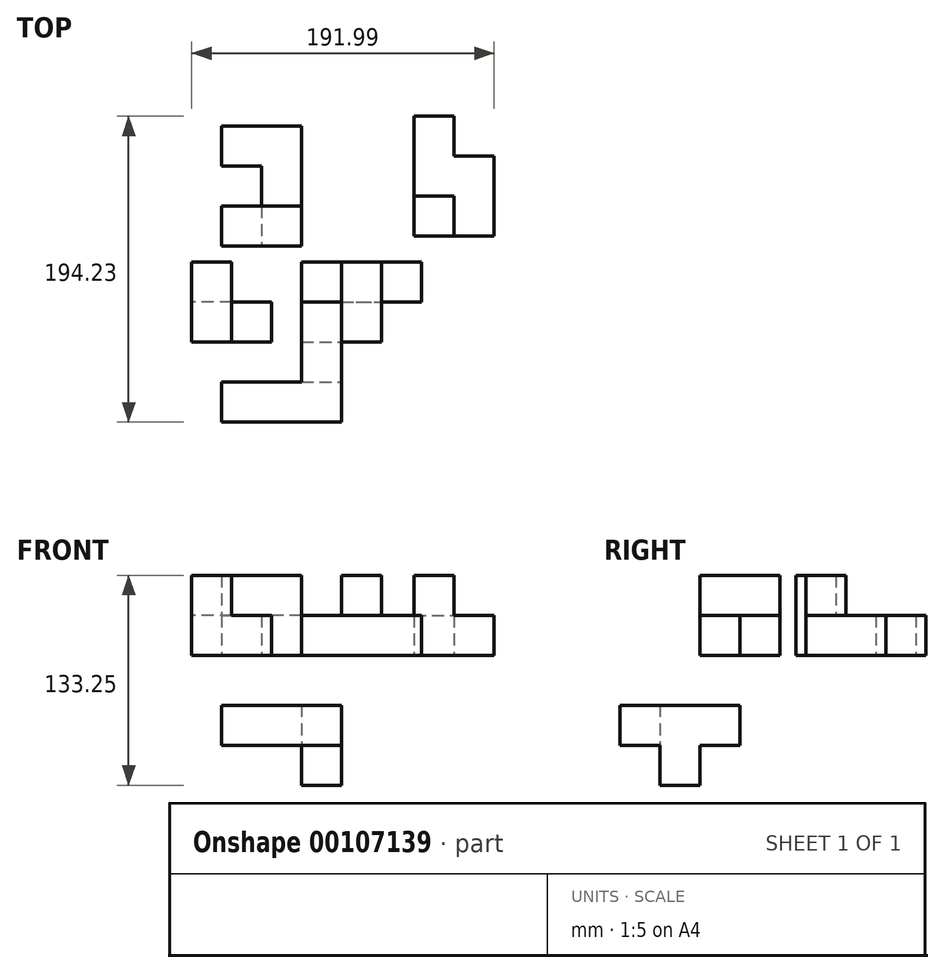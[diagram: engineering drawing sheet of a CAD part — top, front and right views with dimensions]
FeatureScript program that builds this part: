
annotation { "Feature Type Name" : "Feature", "Feature Type Description" : "" }
export const myFeature = defineFeature(function(context is Context, id is Id, definition is map)
    precondition{}
    {
        {
            var Q0;
            Q0=qCreatedBy(makeId("Front.planeOp"),FACE);
            var sketch = newSketch(context, id + "F0", { "sketchPlane" : qUnion([Q0])});
            skLineSegment(sketch, "E0.bottom", {"start": v(-69.75, 25.4) * mm, "end": v(-18.95, 25.4) * mm});
            skLineSegment(sketch, "E0.top", {"start": v(-69.75, 0) * mm, "end": v(-18.95, 0) * mm});
            skLineSegment(sketch, "E0.left", {"start": v(-69.75, 25.4) * mm, "end": v(-69.75, 0) * mm});
            skLineSegment(sketch, "E0.right", {"start": v(-18.95, 25.4) * mm, "end": v(-18.95, 0) * mm});
            skSolve(sketch);
        }
        {
            var Q0;
            Q0=makeQuery(id+"F0.imprint","IMPRINT",FACE,{"disambiguationData":[TD([[makeQuery(id+"F0.imprint","IMPRINT",EDGE,{"derivedFrom":sQuery(id+"F0.wireOp",EDGE,"E0.bottom")}),-1.0]])]});
            extrude(context, id + "F1", {"entities" : qUnion([Q0]), "depth" : 25.4 * mm});
        }
        {
            var Q0;
            Q0=makeQuery(id+"F1.opExtrude","SWEPT_FACE",FACE,{"disambiguationData":[OSD([sQuery(id+"F0.wireOp",EDGE,"E0.bottom")])]});
            var sketch = newSketch(context, id + "F2", { "sketchPlane" : qUnion([Q0])});
            skLineSegment(sketch, "E1.bottom", {"start": v(-69.75, -25.4) * mm, "end": v(-44.35, -25.4) * mm});
            skLineSegment(sketch, "E1.top", {"start": v(-69.75, 0) * mm, "end": v(-44.35, 0) * mm});
            skLineSegment(sketch, "E1.left", {"start": v(-69.75, -25.4) * mm, "end": v(-69.75, 0) * mm});
            skLineSegment(sketch, "E1.right", {"start": v(-44.35, -25.4) * mm, "end": v(-44.35, 0) * mm});
            skSolve(sketch);
        }
        {
            var Q0;
            Q0=makeQuery(id+"F2.imprint","IMPRINT",FACE,{"disambiguationData":[TD([[makeQuery(id+"F2.imprint","IMPRINT",EDGE,{"derivedFrom":sQuery(id+"F2.wireOp",EDGE,"E1.bottom")}),1.0]])]});
            extrude(context, id + "F3", {"entities" : qUnion([Q0]), "operationType" : NewBodyOperationType.ADD, "depth" : 25.4 * mm});
        }
        {
            var Q0;
            Q0=makeQuery(id+"F3.boolean.opBoolean","MERGE",FACE,{"derivedFrom":[makeQuery(id+"F1.opExtrude","CAP_FACE",FACE,{"disambiguationData":[OSD([sQuery(id+"F0.wireOp",EDGE,"E0.bottom"),sQuery(id+"F0.wireOp",EDGE,"E0.top"),sQuery(id+"F0.wireOp",EDGE,"E0.left"),sQuery(id+"F0.wireOp",EDGE,"E0.right")])],"isStart":true}),makeQuery(id+"F3.opExtrude","SWEPT_FACE",FACE,{"disambiguationData":[OSD([sQuery(id+"F2.wireOp",EDGE,"E1.top")])]})]});
            var sketch = newSketch(context, id + "F4", { "sketchPlane" : qUnion([Q0])});
            skLineSegment(sketch, "E2.bottom", {"start": v(44.35, 50.8) * mm, "end": v(69.75, 50.8) * mm});
            skLineSegment(sketch, "E2.top", {"start": v(44.35, 25.4) * mm, "end": v(69.75, 25.4) * mm});
            skLineSegment(sketch, "E2.left", {"start": v(44.35, 50.8) * mm, "end": v(44.35, 25.4) * mm});
            skLineSegment(sketch, "E2.right", {"start": v(69.75, 50.8) * mm, "end": v(69.75, 25.4) * mm});
            skSolve(sketch);
        }
        {
            var Q0;
            Q0=makeQuery(id+"F4.imprint","IMPRINT",FACE,{"disambiguationData":[TD([[makeQuery(id+"F4.imprint","IMPRINT",EDGE,{"derivedFrom":sQuery(id+"F4.wireOp",EDGE,"E2.bottom")}),1.0]])]});
            extrude(context, id + "F5", {"entities" : qUnion([Q0]), "operationType" : NewBodyOperationType.ADD, "depth" : 25.4 * mm});
        }
        {
            var Q0;
            Q0=qCreatedBy(makeId("Front.planeOp"),FACE);
            var sketch = newSketch(context, id + "F6", { "sketchPlane" : qUnion([Q0])});
            skLineSegment(sketch, "E3.bottom", {"start": v(0, 0) * mm, "end": v(76.2, 0) * mm});
            skLineSegment(sketch, "E3.top", {"start": v(0, 25.4) * mm, "end": v(76.2, 25.4) * mm});
            skLineSegment(sketch, "E3.left", {"start": v(0, 0) * mm, "end": v(0, 25.4) * mm});
            skLineSegment(sketch, "E3.right", {"start": v(76.2, 0) * mm, "end": v(76.2, 25.4) * mm});
            skSolve(sketch);
        }
        {
            var Q0;
            Q0=makeQuery(id+"F6.imprint","IMPRINT",FACE,{"disambiguationData":[TD([[makeQuery(id+"F6.imprint","IMPRINT",EDGE,{"derivedFrom":sQuery(id+"F6.wireOp",EDGE,"E3.bottom")}),1.0]])]});
            extrude(context, id + "F7", {"entities" : qUnion([Q0]), "oppositeDirection" : true, "depth" : 25.4 * mm});
        }
        {
            var Q0;
            Q0=makeQuery(id+"F7.opExtrude","SWEPT_FACE",FACE,{"disambiguationData":[OSD([sQuery(id+"F6.wireOp",EDGE,"E3.top")])]});
            var sketch = newSketch(context, id + "F8", { "sketchPlane" : qUnion([Q0])});
            skLineSegment(sketch, "E4.bottom", {"start": v(25.4, 25.4) * mm, "end": v(50.8, 25.4) * mm});
            skLineSegment(sketch, "E4.top", {"start": v(25.4, 0) * mm, "end": v(50.8, 0) * mm});
            skLineSegment(sketch, "E4.left", {"start": v(25.4, 25.4) * mm, "end": v(25.4, 0) * mm});
            skLineSegment(sketch, "E4.right", {"start": v(50.8, 25.4) * mm, "end": v(50.8, 0) * mm});
            skSolve(sketch);
        }
        {
            var Q0;
            Q0=makeQuery(id+"F8.imprint","IMPRINT",FACE,{"disambiguationData":[TD([[makeQuery(id+"F8.imprint","IMPRINT",EDGE,{"derivedFrom":sQuery(id+"F8.wireOp",EDGE,"E4.bottom")}),-1.0]])]});
            extrude(context, id + "F9", {"entities" : qUnion([Q0]), "operationType" : NewBodyOperationType.ADD, "depth" : 25.4 * mm});
        }
        {
            var Q0;
            Q0=makeQuery(id+"F9.boolean.opBoolean","MERGE",FACE,{"derivedFrom":[makeQuery(id+"F7.opExtrude","CAP_FACE",FACE,{"disambiguationData":[OSD([sQuery(id+"F6.wireOp",EDGE,"E3.bottom"),sQuery(id+"F6.wireOp",EDGE,"E3.top"),sQuery(id+"F6.wireOp",EDGE,"E3.left"),sQuery(id+"F6.wireOp",EDGE,"E3.right")])],"isStart":true}),makeQuery(id+"F9.opExtrude","SWEPT_FACE",FACE,{"disambiguationData":[OSD([sQuery(id+"F8.wireOp",EDGE,"E4.top")])]})]});
            var sketch = newSketch(context, id + "F10", { "sketchPlane" : qUnion([Q0])});
            skLineSegment(sketch, "E5.bottom", {"start": v(25.4, 50.8) * mm, "end": v(50.8, 50.8) * mm});
            skLineSegment(sketch, "E5.top", {"start": v(25.4, 25.4) * mm, "end": v(50.8, 25.4) * mm});
            skLineSegment(sketch, "E5.left", {"start": v(25.4, 50.8) * mm, "end": v(25.4, 25.4) * mm});
            skLineSegment(sketch, "E5.right", {"start": v(50.8, 50.8) * mm, "end": v(50.8, 25.4) * mm});
            skSolve(sketch);
        }
        {
            var Q0;
            Q0=makeQuery(id+"F10.imprint","IMPRINT",FACE,{"disambiguationData":[TD([[makeQuery(id+"F10.imprint","IMPRINT",EDGE,{"derivedFrom":sQuery(id+"F10.wireOp",EDGE,"E5.bottom")}),-1.0]])]});
            extrude(context, id + "F11", {"entities" : qUnion([Q0]), "operationType" : NewBodyOperationType.ADD, "depth" : 25.4 * mm});
        }
        {
            var Q0;
            Q0=qCreatedBy(makeId("Front.planeOp"),FACE);
            var sketch = newSketch(context, id + "F12", { "sketchPlane" : qUnion([Q0])});
            skLineSegment(sketch, "E6.bottom", {"start": v(76.2, -32.62) * mm, "end": v(0, -32.62) * mm});
            skLineSegment(sketch, "E6.top", {"start": v(76.2, -58.02) * mm, "end": v(0, -58.02) * mm});
            skLineSegment(sketch, "E6.left", {"start": v(76.2, -32.62) * mm, "end": v(76.2, -58.02) * mm});
            skLineSegment(sketch, "E6.right", {"start": v(0, -32.62) * mm, "end": v(0, -58.02) * mm});
            skSolve(sketch);
        }
        {
            var Q0;
            Q0=makeQuery(id+"F12.imprint","IMPRINT",FACE,{"disambiguationData":[TD([[makeQuery(id+"F12.imprint","IMPRINT",EDGE,{"derivedFrom":sQuery(id+"F12.wireOp",EDGE,"E6.bottom")}),1.0]])]});
            extrude(context, id + "F13", {"entities" : qUnion([Q0]), "depth" : 25.4 * mm});
        }
        {
            var Q0;
            Q0=makeQuery(id+"F13.opExtrude","SWEPT_FACE",FACE,{"disambiguationData":[OSD([sQuery(id+"F12.wireOp",EDGE,"E6.top")])]});
            var sketch = newSketch(context, id + "F14", { "sketchPlane" : qUnion([Q0])});
            skLineSegment(sketch, "E7.bottom", {"start": v(25.4, 25.4) * mm, "end": v(50.8, 25.4) * mm});
            skLineSegment(sketch, "E7.top", {"start": v(25.4, 0) * mm, "end": v(50.8, 0) * mm});
            skLineSegment(sketch, "E7.left", {"start": v(25.4, 25.4) * mm, "end": v(25.4, 0) * mm});
            skLineSegment(sketch, "E7.right", {"start": v(50.8, 25.4) * mm, "end": v(50.8, 0) * mm});
            skSolve(sketch);
        }
        {
            var Q0;
            Q0=makeQuery(id+"F14.imprint","IMPRINT",FACE,{"disambiguationData":[TD([[makeQuery(id+"F14.imprint","IMPRINT",EDGE,{"derivedFrom":sQuery(id+"F14.wireOp",EDGE,"E7.bottom")}),1.0]])]});
            extrude(context, id + "F15", {"entities" : qUnion([Q0]), "operationType" : NewBodyOperationType.ADD, "depth" : 25.4 * mm});
        }
        {
            var Q0;
            Q0=makeQuery(id+"F15.boolean.opBoolean","MERGE",FACE,{"derivedFrom":[makeQuery(id+"F13.opExtrude","CAP_FACE",FACE,{"disambiguationData":[OSD([sQuery(id+"F12.wireOp",EDGE,"E6.bottom"),sQuery(id+"F12.wireOp",EDGE,"E6.top"),sQuery(id+"F12.wireOp",EDGE,"E6.left"),sQuery(id+"F12.wireOp",EDGE,"E6.right")])],"isStart":true}),makeQuery(id+"F15.opExtrude","SWEPT_FACE",FACE,{"disambiguationData":[OSD([sQuery(id+"F14.wireOp",EDGE,"E7.top")])]})]});
            var sketch = newSketch(context, id + "F16", { "sketchPlane" : qUnion([Q0])});
            skLineSegment(sketch, "E8.bottom", {"start": v(0, -32.62) * mm, "end": v(-25.4, -32.62) * mm});
            skLineSegment(sketch, "E8.top", {"start": v(0, -58.02) * mm, "end": v(-25.4, -58.02) * mm});
            skLineSegment(sketch, "E8.left", {"start": v(0, -32.62) * mm, "end": v(0, -58.02) * mm});
            skLineSegment(sketch, "E8.right", {"start": v(-25.4, -32.62) * mm, "end": v(-25.4, -58.02) * mm});
            skSolve(sketch);
        }
        {
            var Q0;
            Q0=makeQuery(id+"F16.imprint","IMPRINT",FACE,{"disambiguationData":[TD([[makeQuery(id+"F16.imprint","IMPRINT",EDGE,{"derivedFrom":sQuery(id+"F16.wireOp",EDGE,"E8.bottom")}),-1.0]])]});
            extrude(context, id + "F17", {"entities" : qUnion([Q0]), "operationType" : NewBodyOperationType.ADD, "depth" : 25.4 * mm});
        }
        {
            var Q0;
            Q0=makeQuery(id+"F13.opExtrude","SWEPT_BODY",BODY,{"disambiguationData":[OSD([sQuery(id+"F12.wireOp",EDGE,"E6.bottom"),sQuery(id+"F12.wireOp",EDGE,"E6.top"),sQuery(id+"F12.wireOp",EDGE,"E6.left"),sQuery(id+"F12.wireOp",EDGE,"E6.right")])]});
            deleteBodies(context, id + "F18", {"entities" : qUnion([Q0])});
        }
        {
            var Q0;
            Q0=qCreatedBy(makeId("Right.planeOp"),FACE);
            var sketch = newSketch(context, id + "F19", { "sketchPlane" : qUnion([Q0])});
            skLineSegment(sketch, "E9.bottom", {"start": v(0, -57.05) * mm, "end": v(-76.2, -57.05) * mm});
            skLineSegment(sketch, "E9.top", {"start": v(0, -31.65) * mm, "end": v(-76.2, -31.65) * mm});
            skLineSegment(sketch, "E9.left", {"start": v(0, -57.05) * mm, "end": v(0, -31.65) * mm});
            skLineSegment(sketch, "E9.right", {"start": v(-76.2, -57.05) * mm, "end": v(-76.2, -31.65) * mm});
            skSolve(sketch);
        }
        {
            var Q0;
            Q0=makeQuery(id+"F19.imprint","IMPRINT",FACE,{"disambiguationData":[TD([[makeQuery(id+"F19.imprint","IMPRINT",EDGE,{"derivedFrom":sQuery(id+"F19.wireOp",EDGE,"E9.bottom")}),-1.0]])]});
            extrude(context, id + "F20", {"entities" : qUnion([Q0]), "depth" : 25.4 * mm});
        }
        {
            var Q0;
            Q0=makeQuery(id+"F20.opExtrude","CAP_FACE",FACE,{"disambiguationData":[OSD([sQuery(id+"F19.wireOp",EDGE,"E9.bottom"),sQuery(id+"F19.wireOp",EDGE,"E9.top"),sQuery(id+"F19.wireOp",EDGE,"E9.left"),sQuery(id+"F19.wireOp",EDGE,"E9.right")])],"isStart":true});
            var sketch = newSketch(context, id + "F21", { "sketchPlane" : qUnion([Q0])});
            skLineSegment(sketch, "E10.bottom", {"start": v(76.2, -31.65) * mm, "end": v(50.8, -31.65) * mm});
            skLineSegment(sketch, "E10.top", {"start": v(76.2, -57.05) * mm, "end": v(50.8, -57.05) * mm});
            skLineSegment(sketch, "E10.left", {"start": v(76.2, -31.65) * mm, "end": v(76.2, -57.05) * mm});
            skLineSegment(sketch, "E10.right", {"start": v(50.8, -31.65) * mm, "end": v(50.8, -57.05) * mm});
            skSolve(sketch);
        }
        {
            var Q0;
            Q0=makeQuery(id+"F21.imprint","IMPRINT",FACE,{"disambiguationData":[TD([[makeQuery(id+"F21.imprint","IMPRINT",EDGE,{"derivedFrom":sQuery(id+"F21.wireOp",EDGE,"E10.bottom")}),-1.0]])]});
            extrude(context, id + "F22", {"entities" : qUnion([Q0]), "operationType" : NewBodyOperationType.ADD, "depth" : 50.8 * mm});
        }
        {
            var Q0;
            Q0=makeQuery(id+"F22.boolean.opBoolean","MERGE",FACE,{"derivedFrom":[makeQuery(id+"F20.opExtrude","SWEPT_FACE",FACE,{"disambiguationData":[OSD([sQuery(id+"F19.wireOp",EDGE,"E9.bottom")])]}),makeQuery(id+"F22.opExtrude","SWEPT_FACE",FACE,{"disambiguationData":[OSD([sQuery(id+"F21.wireOp",EDGE,"E10.top")])]})]});
            var sketch = newSketch(context, id + "F23", { "sketchPlane" : qUnion([Q0])});
            skLineSegment(sketch, "E11.bottom", {"start": v(0, 50.8) * mm, "end": v(25.4, 50.8) * mm});
            skLineSegment(sketch, "E11.top", {"start": v(0, 25.4) * mm, "end": v(25.4, 25.4) * mm});
            skLineSegment(sketch, "E11.left", {"start": v(0, 50.8) * mm, "end": v(0, 25.4) * mm});
            skLineSegment(sketch, "E11.right", {"start": v(25.4, 50.8) * mm, "end": v(25.4, 25.4) * mm});
            skSolve(sketch);
        }
        {
            var Q0;
            Q0=makeQuery(id+"F23.imprint","IMPRINT",FACE,{"disambiguationData":[TD([[makeQuery(id+"F23.imprint","IMPRINT",EDGE,{"derivedFrom":sQuery(id+"F23.wireOp",EDGE,"E11.bottom")}),-1.0]])]});
            extrude(context, id + "F24", {"entities" : qUnion([Q0]), "operationType" : NewBodyOperationType.ADD, "depth" : 25.4 * mm});
        }
        {
            var Q0;
            Q0=qCreatedBy(makeId("Top.planeOp"),FACE);
            var sketch = newSketch(context, id + "F25", { "sketchPlane" : qUnion([Q0])});
            skLineSegment(sketch, "E12.bottom", {"start": v(76.2, -76.2) * mm, "end": v(0, -76.2) * mm});
            skLineSegment(sketch, "E12.top", {"start": v(76.2, -50.8) * mm, "end": v(0, -50.8) * mm});
            skLineSegment(sketch, "E12.left", {"start": v(76.2, -76.2) * mm, "end": v(76.2, -50.8) * mm});
            skLineSegment(sketch, "E12.right", {"start": v(0, -76.2) * mm, "end": v(0, -50.8) * mm});
            skSolve(sketch);
        }
        {
            var Q0;
            Q0=makeQuery(id+"F25.imprint","IMPRINT",FACE,{"disambiguationData":[TD([[makeQuery(id+"F25.imprint","IMPRINT",EDGE,{"derivedFrom":sQuery(id+"F25.wireOp",EDGE,"E12.bottom")}),-1.0]])]});
            extrude(context, id + "F26", {"entities" : qUnion([Q0]), "depth" : 25.4 * mm});
        }
        {
            var Q0;
            Q0=makeQuery(id+"F26.opExtrude","SWEPT_FACE",FACE,{"disambiguationData":[OSD([sQuery(id+"F25.wireOp",EDGE,"E12.top")])]});
            var sketch = newSketch(context, id + "F27", { "sketchPlane" : qUnion([Q0])});
            skLineSegment(sketch, "E13.bottom", {"start": v(-76.2, 25.4) * mm, "end": v(-50.8, 25.4) * mm});
            skLineSegment(sketch, "E13.top", {"start": v(-76.2, 0) * mm, "end": v(-50.8, 0) * mm});
            skLineSegment(sketch, "E13.left", {"start": v(-76.2, 25.4) * mm, "end": v(-76.2, 0) * mm});
            skLineSegment(sketch, "E13.right", {"start": v(-50.8, 25.4) * mm, "end": v(-50.8, 0) * mm});
            skSolve(sketch);
        }
        {
            var Q0;
            Q0=makeQuery(id+"F27.imprint","IMPRINT",FACE,{"disambiguationData":[TD([[makeQuery(id+"F27.imprint","IMPRINT",EDGE,{"derivedFrom":sQuery(id+"F27.wireOp",EDGE,"E13.bottom")}),-1.0]])]});
            extrude(context, id + "F28", {"entities" : qUnion([Q0]), "operationType" : NewBodyOperationType.ADD, "depth" : 25.4 * mm});
        }
        {
            var Q0;
            Q0=makeQuery(id+"F28.boolean.opBoolean","MERGE",FACE,{"derivedFrom":[makeQuery(id+"F26.opExtrude","CAP_FACE",FACE,{"disambiguationData":[OSD([sQuery(id+"F25.wireOp",EDGE,"E12.bottom"),sQuery(id+"F25.wireOp",EDGE,"E12.top"),sQuery(id+"F25.wireOp",EDGE,"E12.left"),sQuery(id+"F25.wireOp",EDGE,"E12.right")])],"isStart":false}),makeQuery(id+"F28.opExtrude","SWEPT_FACE",FACE,{"disambiguationData":[OSD([sQuery(id+"F27.wireOp",EDGE,"E13.bottom")])]})]});
            var sketch = newSketch(context, id + "F29", { "sketchPlane" : qUnion([Q0])});
            skLineSegment(sketch, "E14.bottom", {"start": v(76.2, -76.2) * mm, "end": v(25.4, -76.2) * mm});
            skLineSegment(sketch, "E14.top", {"start": v(76.2, -50.8) * mm, "end": v(25.4, -50.8) * mm});
            skLineSegment(sketch, "E14.left", {"start": v(76.2, -76.2) * mm, "end": v(76.2, -50.8) * mm});
            skLineSegment(sketch, "E14.right", {"start": v(25.4, -76.2) * mm, "end": v(25.4, -50.8) * mm});
            skSolve(sketch);
        }
        {
            var Q0;
            Q0=makeQuery(id+"F29.imprint","IMPRINT",FACE,{"disambiguationData":[TD([[makeQuery(id+"F29.imprint","IMPRINT",EDGE,{"derivedFrom":sQuery(id+"F29.wireOp",EDGE,"E14.bottom")}),-1.0]])]});
            extrude(context, id + "F30", {"entities" : qUnion([Q0]), "operationType" : NewBodyOperationType.ADD, "depth" : 25.4 * mm});
        }
        {
            var Q0;
            Q0=makeQuery(id+"F26.opExtrude","SWEPT_BODY",BODY,{"disambiguationData":[OSD([sQuery(id+"F25.wireOp",EDGE,"E12.bottom"),sQuery(id+"F25.wireOp",EDGE,"E12.top"),sQuery(id+"F25.wireOp",EDGE,"E12.left"),sQuery(id+"F25.wireOp",EDGE,"E12.right")])]});
            deleteBodies(context, id + "F31", {"entities" : qUnion([Q0])});
        }
        {
            var Q0;
            Q0=qCreatedBy(makeId("Top.planeOp"),FACE);
            var sketch = newSketch(context, id + "F32", { "sketchPlane" : qUnion([Q0])});
            skLineSegment(sketch, "E15.bottom", {"start": v(76.2, -76.2) * mm, "end": v(0, -76.2) * mm});
            skLineSegment(sketch, "E15.top", {"start": v(76.2, -50.8) * mm, "end": v(0, -50.8) * mm});
            skLineSegment(sketch, "E15.left", {"start": v(76.2, -76.2) * mm, "end": v(76.2, -50.8) * mm});
            skLineSegment(sketch, "E15.right", {"start": v(0, -76.2) * mm, "end": v(0, -50.8) * mm});
            skSolve(sketch);
        }
        {
            var Q0;
            Q0=makeQuery(id+"F32.imprint","IMPRINT",FACE,{"disambiguationData":[TD([[makeQuery(id+"F32.imprint","IMPRINT",EDGE,{"derivedFrom":sQuery(id+"F32.wireOp",EDGE,"E15.bottom")}),-1.0]])]});
            extrude(context, id + "F33", {"entities" : qUnion([Q0]), "depth" : 25.4 * mm});
        }
        {
            var Q0;
            Q0=makeQuery(id+"F33.opExtrude","SWEPT_FACE",FACE,{"disambiguationData":[OSD([sQuery(id+"F32.wireOp",EDGE,"E15.top")])]});
            var sketch = newSketch(context, id + "F34", { "sketchPlane" : qUnion([Q0])});
            skLineSegment(sketch, "E16.bottom", {"start": v(-76.2, 25.4) * mm, "end": v(-50.8, 25.4) * mm});
            skLineSegment(sketch, "E16.top", {"start": v(-76.2, 0) * mm, "end": v(-50.8, 0) * mm});
            skLineSegment(sketch, "E16.left", {"start": v(-76.2, 25.4) * mm, "end": v(-76.2, 0) * mm});
            skLineSegment(sketch, "E16.right", {"start": v(-50.8, 25.4) * mm, "end": v(-50.8, 0) * mm});
            skSolve(sketch);
        }
        {
            var Q0;
            Q0=makeQuery(id+"F34.imprint","IMPRINT",FACE,{"disambiguationData":[TD([[makeQuery(id+"F34.imprint","IMPRINT",EDGE,{"derivedFrom":sQuery(id+"F34.wireOp",EDGE,"E16.bottom")}),-1.0]])]});
            extrude(context, id + "F35", {"entities" : qUnion([Q0]), "operationType" : NewBodyOperationType.ADD, "depth" : 25.4 * mm});
        }
        {
            var Q0;
            Q0=makeQuery(id+"F35.boolean.opBoolean","MERGE",FACE,{"derivedFrom":[makeQuery(id+"F33.opExtrude","CAP_FACE",FACE,{"disambiguationData":[OSD([sQuery(id+"F32.wireOp",EDGE,"E15.bottom"),sQuery(id+"F32.wireOp",EDGE,"E15.top"),sQuery(id+"F32.wireOp",EDGE,"E15.left"),sQuery(id+"F32.wireOp",EDGE,"E15.right")])],"isStart":false}),makeQuery(id+"F35.opExtrude","SWEPT_FACE",FACE,{"disambiguationData":[OSD([sQuery(id+"F34.wireOp",EDGE,"E16.bottom")])]})]});
            var sketch = newSketch(context, id + "F36", { "sketchPlane" : qUnion([Q0])});
            skLineSegment(sketch, "E17.bottom", {"start": v(0, -76.2) * mm, "end": v(25.4, -76.2) * mm});
            skLineSegment(sketch, "E17.top", {"start": v(0, -50.8) * mm, "end": v(25.4, -50.8) * mm});
            skLineSegment(sketch, "E17.left", {"start": v(0, -76.2) * mm, "end": v(0, -50.8) * mm});
            skLineSegment(sketch, "E17.right", {"start": v(25.4, -76.2) * mm, "end": v(25.4, -50.8) * mm});
            skSolve(sketch);
        }
        {
            var Q0;
            Q0=makeQuery(id+"F36.imprint","IMPRINT",FACE,{"disambiguationData":[TD([[makeQuery(id+"F36.imprint","IMPRINT",EDGE,{"derivedFrom":sQuery(id+"F36.wireOp",EDGE,"E17.bottom")}),-1.0]])]});
            extrude(context, id + "F37", {"entities" : qUnion([Q0]), "operationType" : NewBodyOperationType.ADD, "depth" : 25.4 * mm});
        }
        {
            var Q0;
            Q0=makeQuery(id+"F37.boolean.opBoolean","MERGE",FACE,{"derivedFrom":[makeQuery(id+"F33.opExtrude","SWEPT_FACE",FACE,{"disambiguationData":[OSD([sQuery(id+"F32.wireOp",EDGE,"E15.top")])]}),makeQuery(id+"F37.opExtrude","SWEPT_FACE",FACE,{"disambiguationData":[OSD([sQuery(id+"F36.wireOp",EDGE,"E17.top")])]})]});
            var sketch = newSketch(context, id + "F38", { "sketchPlane" : qUnion([Q0])});
            skLineSegment(sketch, "E18.bottom", {"start": v(-25.4, 50.8) * mm, "end": v(0, 50.8) * mm});
            skLineSegment(sketch, "E18.top", {"start": v(-25.4, 25.4) * mm, "end": v(0, 25.4) * mm});
            skLineSegment(sketch, "E18.left", {"start": v(-25.4, 50.8) * mm, "end": v(-25.4, 25.4) * mm});
            skLineSegment(sketch, "E18.right", {"start": v(0, 50.8) * mm, "end": v(0, 25.4) * mm});
            skSolve(sketch);
        }
        {
            var Q0;
            Q0=makeQuery(id+"F38.imprint","IMPRINT",FACE,{"disambiguationData":[TD([[makeQuery(id+"F38.imprint","IMPRINT",EDGE,{"derivedFrom":sQuery(id+"F38.wireOp",EDGE,"E18.bottom")}),-1.0]])]});
            extrude(context, id + "F39", {"entities" : qUnion([Q0]), "operationType" : NewBodyOperationType.ADD, "depth" : 25.4 * mm});
        }
        {
            var Q0;
            Q0=makeQuery(id+"F33.opExtrude","SWEPT_BODY",BODY,{"disambiguationData":[OSD([sQuery(id+"F32.wireOp",EDGE,"E15.bottom"),sQuery(id+"F32.wireOp",EDGE,"E15.top"),sQuery(id+"F32.wireOp",EDGE,"E15.left"),sQuery(id+"F32.wireOp",EDGE,"E15.right")])]});
            deleteBodies(context, id + "F40", {"entities" : qUnion([Q0])});
        }
        {
            var Q0;
            Q0=qCreatedBy(makeId("Top.planeOp"),FACE);
            var sketch = newSketch(context, id + "F41", { "sketchPlane" : qUnion([Q0])});
            skLineSegment(sketch, "E19.bottom", {"start": v(0, 35.56) * mm, "end": v(-25.4, 35.56) * mm});
            skLineSegment(sketch, "E19.top", {"start": v(0, 111.76) * mm, "end": v(-25.4, 111.76) * mm});
            skLineSegment(sketch, "E19.left", {"start": v(0, 35.56) * mm, "end": v(0, 111.76) * mm});
            skLineSegment(sketch, "E19.right", {"start": v(-25.4, 35.56) * mm, "end": v(-25.4, 111.76) * mm});
            skSolve(sketch);
        }
        {
            var Q0;
            Q0=makeQuery(id+"F41.imprint","IMPRINT",FACE,{"disambiguationData":[TD([[makeQuery(id+"F41.imprint","IMPRINT",EDGE,{"derivedFrom":sQuery(id+"F41.wireOp",EDGE,"E19.bottom")}),-1.0]])]});
            extrude(context, id + "F42", {"entities" : qUnion([Q0]), "depth" : 25.4 * mm});
        }
        {
            var Q0;
            Q0=makeQuery(id+"F42.opExtrude","CAP_FACE",FACE,{"disambiguationData":[OSD([sQuery(id+"F41.wireOp",EDGE,"E19.bottom"),sQuery(id+"F41.wireOp",EDGE,"E19.top"),sQuery(id+"F41.wireOp",EDGE,"E19.left"),sQuery(id+"F41.wireOp",EDGE,"E19.right")])],"isStart":false});
            var sketch = newSketch(context, id + "F43", { "sketchPlane" : qUnion([Q0])});
            skLineSegment(sketch, "E20.bottom", {"start": v(0, 35.56) * mm, "end": v(-25.4, 35.56) * mm});
            skLineSegment(sketch, "E20.top", {"start": v(0, 60.96) * mm, "end": v(-25.4, 60.96) * mm});
            skLineSegment(sketch, "E20.left", {"start": v(0, 35.56) * mm, "end": v(0, 60.96) * mm});
            skLineSegment(sketch, "E20.right", {"start": v(-25.4, 35.56) * mm, "end": v(-25.4, 60.96) * mm});
            skSolve(sketch);
        }
        {
            var Q0;
            Q0=makeQuery(id+"F43.imprint","IMPRINT",FACE,{"disambiguationData":[TD([[makeQuery(id+"F43.imprint","IMPRINT",EDGE,{"derivedFrom":sQuery(id+"F43.wireOp",EDGE,"E20.bottom")}),-1.0]])]});
            extrude(context, id + "F44", {"entities" : qUnion([Q0]), "operationType" : NewBodyOperationType.ADD, "depth" : 25.4 * mm});
        }
        {
            var Q0;
            Q0=makeQuery(id+"F44.boolean.opBoolean","MERGE",FACE,{"derivedFrom":[makeQuery(id+"F42.opExtrude","SWEPT_FACE",FACE,{"disambiguationData":[OSD([sQuery(id+"F41.wireOp",EDGE,"E19.right")])]}),makeQuery(id+"F44.opExtrude","SWEPT_FACE",FACE,{"disambiguationData":[OSD([sQuery(id+"F43.wireOp",EDGE,"E20.right")])]})]});
            var sketch = newSketch(context, id + "F45", { "sketchPlane" : qUnion([Q0])});
            skLineSegment(sketch, "E21.bottom", {"start": v(-60.96, 50.8) * mm, "end": v(-35.56, 50.8) * mm});
            skLineSegment(sketch, "E21.top", {"start": v(-60.96, 25.4) * mm, "end": v(-35.56, 25.4) * mm});
            skLineSegment(sketch, "E21.left", {"start": v(-60.96, 50.8) * mm, "end": v(-60.96, 25.4) * mm});
            skLineSegment(sketch, "E21.right", {"start": v(-35.56, 50.8) * mm, "end": v(-35.56, 25.4) * mm});
            skSolve(sketch);
        }
        {
            var Q0;
            Q0=makeQuery(id+"F45.imprint","IMPRINT",FACE,{"disambiguationData":[TD([[makeQuery(id+"F45.imprint","IMPRINT",EDGE,{"derivedFrom":sQuery(id+"F45.wireOp",EDGE,"E21.bottom")}),1.0]])]});
            extrude(context, id + "F46", {"entities" : qUnion([Q0]), "operationType" : NewBodyOperationType.ADD, "depth" : 25.4 * mm});
        }
        {
            var Q0;
            Q0=makeQuery(id+"F44.boolean.opBoolean","MERGE",FACE,{"derivedFrom":[makeQuery(id+"F42.opExtrude","SWEPT_FACE",FACE,{"disambiguationData":[OSD([sQuery(id+"F41.wireOp",EDGE,"E19.right")])]}),makeQuery(id+"F44.opExtrude","SWEPT_FACE",FACE,{"disambiguationData":[OSD([sQuery(id+"F43.wireOp",EDGE,"E20.right")])]})]});
            var sketch = newSketch(context, id + "F47", { "sketchPlane" : qUnion([Q0])});
            skLineSegment(sketch, "E22.bottom", {"start": v(-111.76, 25.4) * mm, "end": v(-86.36, 25.4) * mm});
            skLineSegment(sketch, "E22.top", {"start": v(-111.76, 0) * mm, "end": v(-86.36, 0) * mm});
            skLineSegment(sketch, "E22.left", {"start": v(-111.76, 25.4) * mm, "end": v(-111.76, 0) * mm});
            skLineSegment(sketch, "E22.right", {"start": v(-86.36, 25.4) * mm, "end": v(-86.36, 0) * mm});
            skSolve(sketch);
        }
        {
            var Q0;
            Q0=makeQuery(id+"F47.imprint","IMPRINT",FACE,{"disambiguationData":[TD([[makeQuery(id+"F47.imprint","IMPRINT",EDGE,{"derivedFrom":sQuery(id+"F47.wireOp",EDGE,"E22.bottom")}),1.0]])]});
            extrude(context, id + "F48", {"entities" : qUnion([Q0]), "operationType" : NewBodyOperationType.ADD, "depth" : 25.4 * mm});
        }
        {
            var Q0;
            Q0=qCreatedBy(makeId("Top.planeOp"),FACE);
            var sketch = newSketch(context, id + "F49", { "sketchPlane" : qUnion([Q0])});
            skLineSegment(sketch, "E23.bottom", {"start": v(122.24, 92.63) * mm, "end": v(71.44, 92.63) * mm});
            skLineSegment(sketch, "E23.top", {"start": v(122.24, 41.83) * mm, "end": v(71.44, 41.83) * mm});
            skLineSegment(sketch, "E23.left", {"start": v(122.24, 92.63) * mm, "end": v(122.24, 41.83) * mm});
            skLineSegment(sketch, "E23.right", {"start": v(71.44, 92.63) * mm, "end": v(71.44, 41.83) * mm});
            skSolve(sketch);
        }
        {
            var Q0;
            Q0=makeQuery(id+"F49.imprint","IMPRINT",FACE,{"disambiguationData":[TD([[makeQuery(id+"F49.imprint","IMPRINT",EDGE,{"derivedFrom":sQuery(id+"F49.wireOp",EDGE,"E23.bottom")}),1.0]])]});
            extrude(context, id + "F50", {"entities" : qUnion([Q0]), "depth" : 25.4 * mm});
        }
        {
            var Q0;
            Q0=makeQuery(id+"F50.opExtrude","CAP_FACE",FACE,{"disambiguationData":[OSD([sQuery(id+"F49.wireOp",EDGE,"E23.bottom"),sQuery(id+"F49.wireOp",EDGE,"E23.top"),sQuery(id+"F49.wireOp",EDGE,"E23.left"),sQuery(id+"F49.wireOp",EDGE,"E23.right")])],"isStart":false});
            var sketch = newSketch(context, id + "F51", { "sketchPlane" : qUnion([Q0])});
            skLineSegment(sketch, "E24.bottom", {"start": v(71.44, 41.83) * mm, "end": v(96.84, 41.83) * mm});
            skLineSegment(sketch, "E24.top", {"start": v(71.44, 67.23) * mm, "end": v(96.84, 67.23) * mm});
            skLineSegment(sketch, "E24.left", {"start": v(71.44, 41.83) * mm, "end": v(71.44, 67.23) * mm});
            skLineSegment(sketch, "E24.right", {"start": v(96.84, 41.83) * mm, "end": v(96.84, 67.23) * mm});
            skSolve(sketch);
        }
        {
            var Q0;
            Q0=makeQuery(id+"F51.imprint","IMPRINT",FACE,{"disambiguationData":[TD([[makeQuery(id+"F51.imprint","IMPRINT",EDGE,{"derivedFrom":sQuery(id+"F51.wireOp",EDGE,"E24.bottom")}),-1.0]])]});
            extrude(context, id + "F52", {"entities" : qUnion([Q0]), "operationType" : NewBodyOperationType.ADD, "depth" : 25.4 * mm});
        }
        {
            var Q0;
            Q0=makeQuery(id+"F50.opExtrude","SWEPT_FACE",FACE,{"disambiguationData":[OSD([sQuery(id+"F49.wireOp",EDGE,"E23.bottom")])]});
            var sketch = newSketch(context, id + "F53", { "sketchPlane" : qUnion([Q0])});
            skLineSegment(sketch, "E25.bottom", {"start": v(-71.44, 25.4) * mm, "end": v(-96.84, 25.4) * mm});
            skLineSegment(sketch, "E25.top", {"start": v(-71.44, 0) * mm, "end": v(-96.84, 0) * mm});
            skLineSegment(sketch, "E25.left", {"start": v(-71.44, 25.4) * mm, "end": v(-71.44, 0) * mm});
            skLineSegment(sketch, "E25.right", {"start": v(-96.84, 25.4) * mm, "end": v(-96.84, 0) * mm});
            skSolve(sketch);
        }
        {
            var Q0;
            Q0=makeQuery(id+"F53.imprint","IMPRINT",FACE,{"disambiguationData":[TD([[makeQuery(id+"F53.imprint","IMPRINT",EDGE,{"derivedFrom":sQuery(id+"F53.wireOp",EDGE,"E25.bottom")}),-1.0]])]});
            extrude(context, id + "F54", {"entities" : qUnion([Q0]), "operationType" : NewBodyOperationType.ADD, "depth" : 25.4 * mm});
        }
    });
